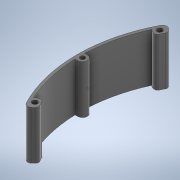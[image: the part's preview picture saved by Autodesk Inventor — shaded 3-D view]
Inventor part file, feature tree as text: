
AUTODESK INVENTOR PART (.ipt)
format: ipt  version: 2020 (Build 240168000, 168)  size: 1,061,376 bytes
history: native  units: mm
features: extrude x12, sketch x9, projected_geometry x9, other x3, fillet x2
ambient origin geometry x8: Origin, YZ Plane, XZ Plane, XY Plane, X Axis, Y Axis, Z Axis, Center Point
bodies: Body1 (feature_tree)
feature tree (35):
  other  "Твердое тело1"
  extrude  "outer"  TaperAngle=45.0deg  [1 undecoded]
  extrude  "inner"  Depth=7.0mm
  sketch  "Эскиз3"
  extrude  "Выдавливание3"  Depth=20.0mm
  extrude  "Выдавливание4"  Depth=7.0mm
  sketch  "Эскиз4"
  extrude  "Выдавливание5"  Depth=3.2mm
  extrude  "Выдавливание6"  Depth=59.0mm
  sketch  "Эскиз5"
  extrude  "Выдавливание7"  Depth=83.0mm
  extrude  "Выдавливание8"  Depth=69.0mm
  sketch  "Эскиз6"
  extrude  "Выдавливание9"  Depth=55.0mm
  extrude  "Выдавливание10"  Depth=3.0mm
  fillet  "Сопряжение1"  Radius=8.0mm
  other  "РабПлоскость2"
  sketch  "Эскиз8"
  extrude  "Выдавливание11"  Depth=5.0mm
  fillet  "Сопряжение2"  Radius=2.0mm
  sketch  "3D эскиз1"
  extrude  "Выдавливание12"  Depth=40.0mm TaperAngle=360.0deg
  sketch  "Эскиз1"
  sketch  "Эскиз2"
  projected_geometry  "Спроецированная петля1"
  projected_geometry  "Спроецированная петля2"
  projected_geometry  "Спроецированная петля3"
  projected_geometry  "Спроецированная петля4"
  projected_geometry  "Спроецированная петля5"
  projected_geometry  "Спроецированная петля8"
  projected_geometry  "Спроецированная петля9"
  projected_geometry  "Спроецированная петля10"
  other  "Проецирование на поверхность1"
  sketch  "Эскиз10"
  projected_geometry  "Спроецированная петля11"
note: 1 required parameter value undecoded (feature->parameter linkage not recoverable at this tier; creation-order binding heuristic only, values carry confidence <= 0.55)
